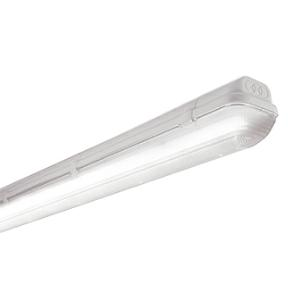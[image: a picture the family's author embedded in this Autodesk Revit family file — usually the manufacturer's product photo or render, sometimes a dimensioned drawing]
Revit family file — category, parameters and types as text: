
# Revit family: 3f_filippi_-_3f_linda_basic_3f_filippi_-_58767_-_3f_linda_led_basic_st_2x20w_l1570
name_source: partatom
category: Lighting Fixtures
units: mm (PartAtom-declared; Revit-internal decimal feet)

## family parameters
Cut with Voids When Loaded = No
Host = Face
Light Source = No
Part Type = Normal
Room Calculation Point = No
Round Connector Dimension = Use Diameter
Shared = No

## types (1)
- 3F Filippi - 3F Linda Basic (1 x LED, 6281 lm, 41 W, 4000 K)
    Apparent Load = 41 VA
    Approval mark = CE
    CIE Flux Codes = 43 74 92 95 100
    Color Rendering = 80
    Color Temperature = 4000 K
    Control Gear = Electronic ballast
    Default Elevation = 1800 mm
    Description = ILLUMINOTECHNICAL
Luminous efficiency 100% (DLOR 95%, ULOR 5%).
Initial luminous flux of the luminaire 6281 lm.
Controlled symmetric distribution.
Installation Interdistance Transv.D = 1.05 x hu - Long.D = 1.20 x hu.
Tabular UGR (CIE 117 - 4H-8H; S=0.25H; 70/50/20): RUG 23.9 - 22.1.
Beam angle: 127° - 100°.
Luminous efficacy 153 lm/W.
Lifetime (L92/B10): 30000 h. (tq+25°C)
Lifetime (L85/B10): 50000 h. (tq+25°C)
Lifetime (L75/B10): 80000 h. (tq+25°C)
Lifetime (L70/B10): 100000 h. (tq+25°C)
Lifetime (L75/B10): 50000 h. (tq+35°C)
Sudden decreased luminous flux after 50000 hours: 0% (C0).
Photobiological safety in compliance with IEC/TR 62778: RG0 risk exempt, (IEC 62471).
In compliance with IEC/EN 62722-2-1 - IEC/EN 62717 standards.

SOURCE
2 linear LED modules 20W/840.
Energy efficiency class (UE 2019/2020 - UE 2019/2015): D.
CIE 13.3 Colour rendering index: CRI >80 (R9 <50%).
IES TM-30 Fidelity Index: Rf = 84 Rg = 95.
CCT nominal colour temperature 4000 K.
Colour initial tolerance (MacAdam): SDCM 3.

MECHANICAL
Self-extinguishing V2 polycarbonate housing, injection moulded, RAL 7035 grey.
Ecologic anti-aging injected sealing gasket.
Diffuser in self-extinguishing V2 polycarbonate, photo-engraved interior, UV stabilised, injection moulded with smooth outer surface, tamper-proof opening.
Gear-holder reflector in hot-dip galvanised steel, painted with white polyester base.
Snug fit snap-lock clips for diffuser mounting, in polycarbonate.
Fixing brackets in stainless steel.
Possibility for technicians to access the interior of the luminaire.
CSI certificate for food-preparation environments.
Luminaire with limited surface temperature. - D - (EN 60598-2-24)
Dimensions: 1570x100 mm, height 100 mm. Weight 2.43 kg.
IP66 protection degree.
Mechanical strength to impacts IK10 (20 joule).
Glow-wire test resistance 850°C.

ELECTRICAL
Halogen Free electronic wiring 230V-50/60Hz, power factor 0.95, THD <25%, constant output current, SELV, class I, 1 driver.
Power of the luminaire 41 W.
ENEC - CE.
SAFE FLICKER: PstLM=<1 and SVM=<0.4 (IEC TR 61547-1 and IEC TR 63158), to ensure a more comfortable and safe light.
Luminaire compliant with EN 60598-2-22 for power supply from a centralised emergency system CPSS (Central Power Supply System), not incorporated in the luminaire - high risk areas excluded. The default power and flux are 100% in AC and 100% in DC.
Ambient temperature from -20°C to +35°C.
Temperature class T6 max 85°C.
Relative humidity UR: <85%.

INSTALLATION
Ceiling / Suspended / Wall.
All accessories dedicated to this product are available on the Catalog and on our website www.3F-Filippi.com.

APPLICATIONS
Suitable product for food production plants (HACCP), IFS (Food Version 6), BRC (GSFS Food Version 7).
Dry, dusty indoor environments, subject to occasional water splashes.
Virtually shatterproof polycarbonate compatibly with the fumes / atmospheres that compromise the elasticity of plastic materials.
Not suitable for installation on surfaces subject to important vibrations, exposed to weather conditions, on ropes or poles.
Suitable for illumination of public car parks and parking grounds referred to DIN 67528:2018-04.

WARNING
Fixture not suitable for cold stores with an ambient temperature <0°C and/or relative humidity >85%.
Luminaire designed for disposal/recycling at end-of-life.
Replaceable (LED only) light source by a professional. Replaceable control gear by a professional.
    Height = 100 mm  [stored 0.328084 ft]
    Lamp = 1 x LED
    Lamp Light Flux = 6281 lm
    Lamp Power = 41 W
    Lamp count = 1
    Length = 1570 mm
    Lifetime = 50000 h
    Luminous efficacy = 153 lm/W
    Manufacturer = 3F Filippi
    ModVariant = No
    Model = 3F Filippi - 58767 - 3F Linda LED Basic ST 2x20W L1570
    Mounting Place = Ceiling
    Mounting Type = Pendant
    Number of Poles = 1
    OnlyDefault = Yes
    Power Factor = 1
    Product Name = 3F Filippi - 3F Linda Basic
    Product group = pendant luminaire
    ProductGroupID = 9
    Protection Class = Protection class I
    Protection Degree = IP 66
    RLX_Detail_Level = 1
    RLX_Emergency_Light_Flux = 0 lm
    RLX_Emergency_Type = 0
    RLX_Emergency_Type_DB = No
    RlxData = <blob elided: 67637 chars, md5=5bacb11e>
    Socket = socket
    Standby Power = 0 W
    System Light Flux = 6281 lm
    System Power = 41 W
    Type Comments = Product without accessories
    Type Image = 3ffilippi_3f_linda_led_basic_st_2x.jpg
    URL = http://relux.com
    VarID = ---
    Voltage = 0 V
    Weight = 0.00 kg
    Width = 100 mm  [stored 0.328084 ft]

note: [stored X ft] marks values corroborated as IEEE doubles in the binary element streams (Revit-internal decimal feet)

## geometry (parser evidence)
native form markers: Blend x4, Sweep x11
no freeform markers — native parametric forms only
